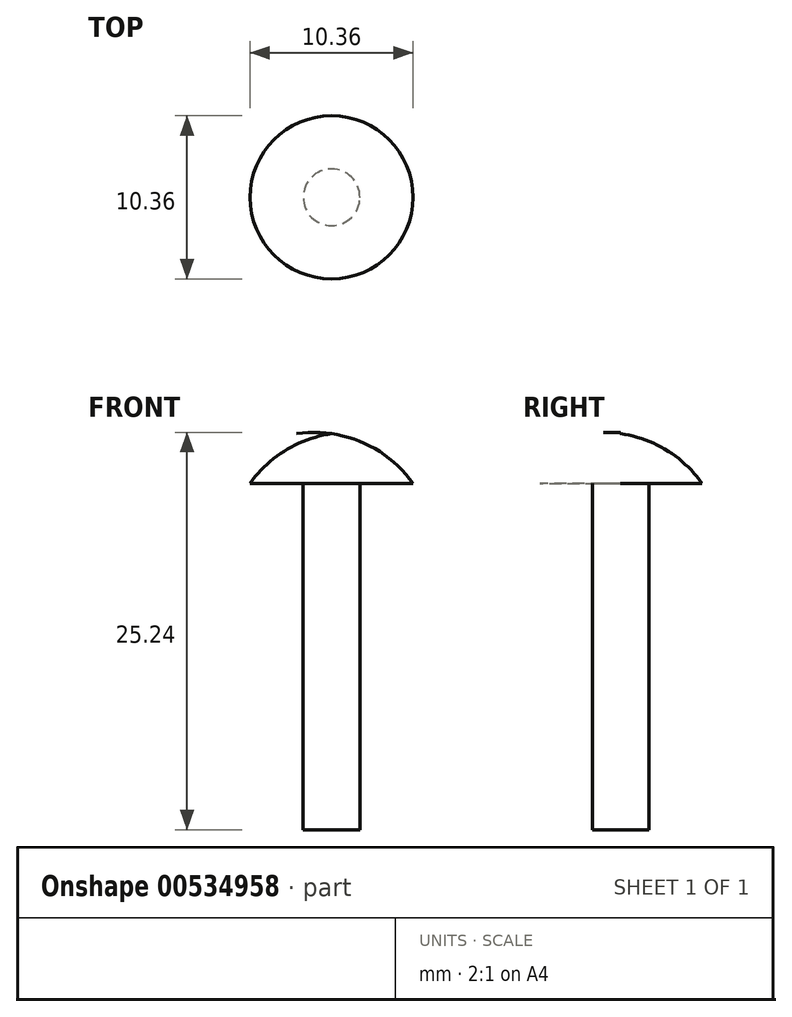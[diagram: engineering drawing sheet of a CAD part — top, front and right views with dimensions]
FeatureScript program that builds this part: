
annotation { "Feature Type Name" : "Feature", "Feature Type Description" : "" }
export const myFeature = defineFeature(function(context is Context, id is Id, definition is map)
    precondition{}
    {
        {
            var Q0;
            Q0=qCreatedBy(makeId("Top.planeOp"),FACE);
            var sketch = newSketch(context, id + "F0", { "sketchPlane" : qUnion([Q0])});
            skCircle(sketch, "E0", {"center": v(0, 0) * mm, "radius": 1.8 * mm});
            skSolve(sketch);
        }
        {
            var Q0;
            Q0 = qSketchRegion(id + "F0", true);
            extrude(context, id + "F1", {"entities" : qUnion([Q0]), "depth" : 22 * mm, "offsetDistance" : 25 * mm});
        }
        {
            var Q0;
            Q0=qCreatedBy(makeId("Front.planeOp"),FACE);
            var sketch = newSketch(context, id + "F2", { "sketchPlane" : qUnion([Q0])});
            skLineSegment(sketch, "E1", {"start": v(0, 22) * mm, "end": v(0, 25.16) * mm});
            skLineSegment(sketch, "E2", {"start": v(0, 22) * mm, "end": v(5.18, 22) * mm});
            skArc(sketch, "E3", {"start": v(5.18, 22) * mm, "mid": v(2.91, 24.1) * mm, "end": v(0, 25.16) * mm});
            skSolve(sketch);
        }
        {
            var Q0;
            Q0=makeQuery(id+"F2.imprint","IMPRINT",FACE,{"disambiguationData":[TD([[makeQuery(id+"F2.imprint","IMPRINT",EDGE,{"derivedFrom":sQuery(id+"F2.wireOp",EDGE,"E1")}),-1.0]])]});
            var Q1;
            Q1=sQuery(id+"F2.wireOp",EDGE,"E1");
            revolve(context, id + "F3", {"operationType" : NewBodyOperationType.ADD, "entities" : qUnion([Q0]), "axis" : qUnion([Q1]), "revolveType" : RevolveType.FULL});
        }
    });
